FCSTD DOCUMENT  (FreeCAD 0.21R33694 (Git))
Label: asanoha_assembly
License: All rights reserved
LicenseURL: http://en.wikipedia.org/wiki/All_rights_reserved
objects: App::Link×6, App::Part×2
EXTERNAL_REF file=../master_kumiko_box.FCStd obj=Spreadsheet
EXTERNAL_REF file=../parts/kumiko/kumiko_inlay_diagonal.FCStd obj=Body063
EXTERNAL_REF file=../parts/kumiko/kumiko_inlay_hindge.FCStd obj=Body062
EXTERNAL_REF file=../parts/kumiko/kumiko_inlay_short_diagonal.FCStd obj=Body064

FEATURE [App::Link] Link  label="SpreadSheet"
  LinkedObject = -> <external ../master_kumiko_box.FCStd>#Spreadsheet
FEATURE [App::Link] Link001  label="long_diagonal"
  LinkedObject = -> <external ../parts/kumiko/kumiko_inlay_diagonal.FCStd>#Body063
FEATURE [App::Link] Link004  label="hindge_body001"
  LinkPlacement = pos=(2.12132,0,11) rot=(1,1,0;3.14159rad)
  LinkedObject = -> <external ../parts/kumiko/kumiko_inlay_hindge.FCStd>#Body062
  Placement = pos=(2.12132,0,11) rot=(1,1,0;3.14159rad)
  expr: .Placement.Base.x = <<SpreadSheet>>.kumiko_thickness / sqrt(2)
  expr: .Placement.Base.y = 0
  expr: .Placement.Base.z = <<SpreadSheet>>.kumiko_hight
FEATURE [App::Link] Link005  label="short_diagonal001"
  LinkPlacement = pos=(24.5,0,0) rot=(0,0,1;3.14159rad)
  LinkedObject = -> <external ../parts/kumiko/kumiko_inlay_short_diagonal.FCStd>#Body064
  Placement = pos=(24.5,0,0) rot=(0,0,1;3.14159rad)
  expr: .Placement.Base.x = <<SpreadSheet>>.kumiko_grid_size - <<SpreadSheet>>.kumiko_thickness
FEATURE [App::Link] Link006  label="hindge_body002"
  LinkPlacement = pos=(24.5,22.3787,0) rot=(0,0,1;3.14159rad)
  LinkedObject = -> <external ../parts/kumiko/kumiko_inlay_hindge.FCStd>#Body062
  Placement = pos=(24.5,22.3787,0) rot=(0,0,1;3.14159rad)
  expr: .Placement.Base.x = <<SpreadSheet>>.kumiko_grid_size - <<SpreadSheet>>.kumiko_thickness
  expr: .Placement.Base.y = <<SpreadSheet>>.kumiko_grid_size - <<SpreadSheet>>.kumiko_thickness - <<SpreadSheet>>.kumiko_thickness / sqrt(2)
FEATURE [App::Part] Part  label="inlay_top_left"
  Group = -> [Link006,Link005,Link004]
  Origin = -> Origin
  Placement = pos=(0,0,11) rot=(1,1,0;3.14159rad)
  expr: .Placement.Base.z = <<SpreadSheet>>.kumiko_hight
FEATURE [App::Link] Link007  label="inlay_bottom_right"
  LinkedObject = -> Part
FEATURE [App::Part] Part001  label="asanoha"
  Group = -> [Link007,Part,Link001]
  Origin = -> Origin001

RESOLVED EXTERNAL PARTS (link-assembly join: the EXTERNAL_REF files above that resolve inside this repo's crawl, each included once):
---- part ../master_kumiko_box.FCStd = doc fcstd_d57fc246fb5e ----
FCSTD DOCUMENT  (FreeCAD 0.21R33771 (Git))
Label: master_kumiko_box
License: All rights reserved
LicenseURL: https://en.wikipedia.org/wiki/All_rights_reserved
objects: App::Link×3, App::Part×2, Spreadsheet::Sheet×1
EXTERNAL_REF file=assembly/box_assembly.FCStd obj=Part
EXTERNAL_REF file=assembly/lid_assembly.FCStd obj=Part
EXTERNAL_REF file=assembly/kumiko_assembly.FCStd obj=Part001

FEATURE [Spreadsheet::Sheet] Spreadsheet  label="SpreadSheet"
  cells = A1='name; B1='value; C1='calc (y/n); A2='box_length; B2(box_length)=130; C2='n; A3='box_width; B3(box_width)==B2 / 2 + B5 - B13 / 2; C3='n; A4='box_height; B4(box_height)=60; C4='y; A5='box_thickness; B5(box_thickness)=11.5; C5='y; A7='lid_height; B7(lid_height)==B8 * 17 / 8.5; C7='y; A8='lid_frame_width; B8(lid_frame_width)==B5 - B13; C8='y; A9='lid_lip_width; B9(lid_lip_width)==B5 - B8; C9='y; A10='lid_lip_height; B10(lid_lip_hight)=3; C10='y; A12='kumiko_hight; B12(kumiko_hight)==B7 * 11 / 17; C12='y; A13='kumiko_thickness; B13(kumiko_thickness)=3; C13='n; A14='kumiko_grid_size; B14(kumiko_grid_size)==(B2 - 2 * B8 - B13) / 4; C14='y; A16='box_wall_height; B16(box_wall_height)==B4 - B7 - B18; C16='y; A18='floor_edge; B18(floor_edge)=2; C18='n; A20='cnc_spacing; B20(cnc_spacing)=0; C20='y
FEATURE [App::Link] Link  label="box"
  LinkedObject = -> <external assembly/box_assembly.FCStd>#Part
FEATURE [App::Link] Link001  label="lid"
  LinkPlacement = pos=(0,0,43) rot=(0,0,1;0rad)
  LinkedObject = -> <external assembly/lid_assembly.FCStd>#Part
  Placement = pos=(0,0,43) rot=(0,0,1;0rad)
  expr: .Placement.Base.z = <<SpreadSheet>>.box_height - <<SpreadSheet>>.lid_height
FEATURE [App::Link] Link002  label="kumiko_assembly"
  LinkPlacement = pos=(8.5,8.5,49) rot=(0,0,1;0rad)
  LinkedObject = -> <external assembly/kumiko_assembly.FCStd>#Part001
  Placement = pos=(8.5,8.5,49) rot=(0,0,1;0rad)
  expr: .Placement.Base.x = <<SpreadSheet>>.lid_frame_width
  expr: .Placement.Base.y = <<SpreadSheet>>.lid_frame_width
  expr: .Placement.Base.z = <<SpreadSheet>>.box_height - Spreadsheet.kumiko_hight
FEATURE [App::Part] Part  label="lid_complete"
  Group = -> [Link002,Link001]
  Origin = -> Origin
FEATURE [App::Part] Part001  label="kumiko_box_complete"
  Group = -> [Part,Link]
  Origin = -> Origin001
---- part ../parts/kumiko/kumiko_inlay_diagonal.FCStd = doc fcstd_409b1c9e1d78 ----
FCSTD DOCUMENT  (FreeCAD 0.21R33694 (Git))
Label: kumiko_inlay_diagonal
License: All rights reserved
LicenseURL: https://en.wikipedia.org/wiki/All_rights_reserved
objects: Sketcher::SketchObject×1, PartDesign::Pad×1, PartDesign::Body×1, App::Link×1
note: 4 computed .brp shape members not serialized (recipe doc carries the construction recipe); baked Part::Feature solids carry a one-line shape summary decoded from their .brp
EXTERNAL_REF file=../../master_kumiko_box.FCStd obj=Spreadsheet

FEATURE [Sketcher::SketchObject] Sketch098  label="long_diagonal_profile"
  FullyConstrained = true
  MapMode = 5
  Support = -> [XY_Plane084]
  expr: Constraints[10] = <<SpreadSheet>>.kumiko_thickness * sqrt(2) / 2
  expr: Constraints[13] = <<SpreadSheet>>.kumiko_thickness * sqrt(2) / 2
  expr: Constraints[1] = 0
  expr: Constraints[2] = 0
  expr: Constraints[3] = <<SpreadSheet>>.kumiko_thickness * sqrt(2) / 2
  expr: Constraints[6] = <<SpreadSheet>>.kumiko_thickness * sqrt(2) / 2
  expr: Constraints[8] = <<SpreadSheet>>.kumiko_grid_size - <<SpreadSheet>>.kumiko_thickness
  expr: Constraints[9] = <<SpreadSheet>>.kumiko_grid_size - <<SpreadSheet>>.kumiko_thickness
  sketch-geometry (6):
    g0: LineSegment StartX=3.6e-15 StartY=0 StartZ=0 EndX=3.6e-15 EndY=2.12132 EndZ=0
    g1: LineSegment StartX=3.6e-15 StartY=0 StartZ=0 EndX=2.12132 EndY=0 EndZ=0
    g2: LineSegment StartX=24.5 StartY=24.5 StartZ=0 EndX=24.5 EndY=22.3787 EndZ=0
    g3: LineSegment StartX=24.5 StartY=24.5 StartZ=0 EndX=22.3787 EndY=24.5 EndZ=0
    g4: LineSegment StartX=2.12132 StartY=0 StartZ=0 EndX=24.5 EndY=22.3787 EndZ=0
    g5: LineSegment StartX=22.3787 StartY=24.5 StartZ=0 EndX=3.6e-15 EndY=2.12132 EndZ=0
  constraints (18):
    c: Vertical(g0)
    c: DistanceY(g-1,g0) = 0
    c: DistanceX(g-1,g0) = 0
    c: DistanceY(g0,g0) = 2.12132
    c: Coincident(g1,g0)
    c: Horizontal(g1)
    c: DistanceX(g1,g1) = 2.12132
    c: Vertical(g2)
    c: DistanceX(g-1,g2) = 24.5
    c: DistanceY(g-1,g2) = 24.5
    c: DistanceY(g2,g2) = 2.12132
    c: Coincident(g3,g2)
    c: Horizontal(g3)
    c: DistanceX(g3,g3) = 2.12132
    c: Coincident(g4,g1)
    c: Coincident(g4,g2)
    c: Coincident(g5,g3)
    c: Coincident(g5,g0)
FEATURE [PartDesign::Pad] Pad047  label="long_diagonal_extrusion"
  Direction = (0,0,1)
  Length = 11
  Length2 = 10
  Profile = -> Sketch098
  ReferenceAxis = -> Sketch098 [N_Axis]
  Type = 0
  expr: Length = <<SpreadSheet>>.kumiko_hight
FEATURE [PartDesign::Body] Body063  label="long_diagonal_body"
  Group = -> [Sketch098,Pad047]
  Origin = -> Origin084
  Tip = -> Pad047
  expr: .Placement.Base.z = 0
FEATURE [App::Link] Link  label="SpreadSheet"
  LinkedObject = -> <external ../../master_kumiko_box.FCStd>#Spreadsheet
---- part ../parts/kumiko/kumiko_inlay_hindge.FCStd = doc fcstd_16ac07aace51 ----
FCSTD DOCUMENT  (FreeCAD 0.21R33694 (Git))
Label: kumiko_inlay_hindge
License: All rights reserved
LicenseURL: https://en.wikipedia.org/wiki/All_rights_reserved
objects: Sketcher::SketchObject×1, PartDesign::Pad×1, PartDesign::Body×1, App::Link×1
note: 4 computed .brp shape members not serialized (recipe doc carries the construction recipe); baked Part::Feature solids carry a one-line shape summary decoded from their .brp
EXTERNAL_REF file=../../master_kumiko_box.FCStd obj=Spreadsheet

FEATURE [Sketcher::SketchObject] Sketch097  label="hindge_drawing"
  FullyConstrained = true
  MapMode = 5
  Support = -> [XY_Plane083]
  expr: Constraints[0] = 0
  expr: Constraints[11] = <<SpreadSheet>>.kumiko_grid_size * (1 - 1 / sqrt(2)) - 1 / 2 * <<SpreadSheet>>.kumiko_thickness
  expr: Constraints[12] = <<SpreadSheet>>.kumiko_grid_size / sqrt(2) - <<SpreadSheet>>.kumiko_thickness * (1 + 1 / sqrt(2)) * 1 / sqrt(2)
  expr: Constraints[18] = 45
  expr: Constraints[1] = 0
  expr: Constraints[2] = 135 °
  expr: Constraints[4] = 2 * 22.5
  expr: Constraints[6] = <<SpreadSheet>>.kumiko_thickness
  expr: Constraints[7] = (<<SpreadSheet>>.kumiko_grid_size - <<SpreadSheet>>.kumiko_thickness * (1 + sqrt(2) + 1 / sqrt(2 - sqrt(2)))) * 1 / sqrt(2)
  expr: Constraints[8] = (<<SpreadSheet>>.kumiko_grid_size - <<SpreadSheet>>.kumiko_thickness * (1 + sqrt(2) + 1 / sqrt(2 - sqrt(2)))) * (1 - 1 / sqrt(2))
  sketch-geometry (8):
    g0: LineSegment StartX=0 StartY=0 StartZ=0 EndX=2.77164 EndY=2.77164 EndZ=0
    g1: LineSegment StartX=0 StartY=0 StartZ=0 EndX=-2e-16 EndY=3.91969 EndZ=0
    g2: GeomPoint X=4.78519 Y=15.4722 Z=0
    g3: LineSegment StartX=-2e-16 StartY=3.91969 StartZ=0 EndX=4.78519 EndY=15.4722 EndZ=0
    g4: GeomPoint X=6.55456 Y=15.8241 Z=0
    g5: LineSegment StartX=4.78519 StartY=15.4722 StartZ=0 EndX=6.55456 EndY=15.8241 EndZ=0
    g6: LineSegment StartX=2.77164 StartY=2.77164 StartZ=0 EndX=7.70261 EndY=14.6761 EndZ=0
    g7: LineSegment StartX=6.55456 StartY=15.8241 StartZ=0 EndX=7.70261 EndY=14.6761 EndZ=0
  constraints (20):
    c: DistanceX(g-1,g0) = 0
    c: DistanceY(g-1,g0) = 0
    c: Angle(g0,g-1) = 2.35619
    c: Coincident(g1,g0)
    c: Angle(g0,g1) = 0.785398
    c: Equal(g1,g0)
    c: Distance(g0,g1) = 3
    c: DistanceY(g1,g2) = 11.5525
    c: DistanceX(g1,g2) = 4.78519
    c: Coincident(g3,g1)
    c: Coincident(g3,g2)
    c: DistanceX(g0,g4) = 6.55456
    c: DistanceY(g0,g4) = 15.8241
    c: Coincident(g5,g3)
    c: Coincident(g5,g4)
    c: Coincident(g6,g0)
    c: Parallel(g3,g6)
    c: Coincident(g7,g5)
    c: Angle(g7,g-1) = 0.785398
    c: Coincident(g7,g6)
FEATURE [PartDesign::Pad] Pad049  label="hindge_extrude"
  Direction = (0,0,1)
  Length = 11
  Length2 = 10
  Profile = -> Sketch097
  ReferenceAxis = -> Sketch097 [N_Axis]
  Type = 0
  expr: Length = <<SpreadSheet>>.kumiko_hight
FEATURE [PartDesign::Body] Body062  label="hindge_body"
  Group = -> [Sketch097,Pad049]
  Origin = -> Origin083
  Tip = -> Pad049
  expr: .Placement.Base.z = 0
FEATURE [App::Link] Link  label="SpreadSheet"
  LinkedObject = -> <external ../../master_kumiko_box.FCStd>#Spreadsheet
---- part ../parts/kumiko/kumiko_inlay_short_diagonal.FCStd = doc fcstd_d7b73f897647 ----
FCSTD DOCUMENT  (FreeCAD 0.21R33694 (Git))
Label: kumiko_inlay_short_diagonal
License: All rights reserved
LicenseURL: https://en.wikipedia.org/wiki/All_rights_reserved
objects: Sketcher::SketchObject×1, PartDesign::Pad×1, PartDesign::Body×1, App::Link×1
note: 4 computed .brp shape members not serialized (recipe doc carries the construction recipe); baked Part::Feature solids carry a one-line shape summary decoded from their .brp
EXTERNAL_REF file=../../master_kumiko_box.FCStd obj=Spreadsheet

FEATURE [Sketcher::SketchObject] Sketch099  label="short_diagonal_drawing"
  FullyConstrained = true
  MapMode = 5
  Support = -> [XY_Plane085]
  expr: Constraints[0] = 0
  expr: Constraints[10] = <<SpreadSheet>>.kumiko_thickness / sqrt(2)
  expr: Constraints[11] = (<<SpreadSheet>>.kumiko_grid_size - <<SpreadSheet>>.kumiko_thickness * (1 + sqrt(2) + 1 / sqrt(2 - sqrt(2)))) * (1 - 1 / sqrt(2))
  expr: Constraints[12] = (<<SpreadSheet>>.kumiko_grid_size - <<SpreadSheet>>.kumiko_thickness * (1 + sqrt(2) + 1 / sqrt(2 - sqrt(2)))) * (1 - 1 / sqrt(2))
  expr: Constraints[21] = 0 mm
  expr: Constraints[3] = <<SpreadSheet>>.kumiko_thickness * sqrt(2) / 2
  expr: Constraints[4] = <<SpreadSheet>>.kumiko_grid_size * (1 - 1 / sqrt(2)) - 1 / 2 * <<SpreadSheet>>.kumiko_thickness
  expr: Constraints[5] = <<SpreadSheet>>.kumiko_grid_size * (1 - 1 / sqrt(2)) - 1 / 2 * <<SpreadSheet>>.kumiko_thickness
  expr: Constraints[6] = (<<SpreadSheet>>.kumiko_grid_size - <<SpreadSheet>>.kumiko_thickness * (1 + sqrt(2) + 1 / sqrt(2 - sqrt(2)))) * (1 - 1 / sqrt(2))
  expr: Constraints[7] = (<<SpreadSheet>>.kumiko_grid_size - <<SpreadSheet>>.kumiko_thickness * (1 + sqrt(2) + 1 / sqrt(2 - sqrt(2)))) * (1 - 1 / sqrt(2))
  sketch-geometry (10):
    g0: GeomPoint X=0 Y=0 Z=0
    g1: LineSegment StartX=0 StartY=0 StartZ=0 EndX=0 EndY=-2.12132 EndZ=0
    g2: GeomPoint X=6.55456 Y=-6.55456 Z=0
    g3: GeomPoint X=4.78519 Y=-6.90651 Z=0
    g4: LineSegment StartX=0 StartY=0 StartZ=0 EndX=2.12132 EndY=0 EndZ=0
    g5: GeomPoint X=6.90651 Y=-4.78519 Z=0
    g6: LineSegment StartX=6.90651 StartY=-4.78519 StartZ=0 EndX=2.12132 EndY=0 EndZ=0
    g7: LineSegment StartX=6.90651 StartY=-4.78519 StartZ=0 EndX=6.55456 EndY=-6.55456 EndZ=0
    g8: LineSegment StartX=6.55456 StartY=-6.55456 StartZ=0 EndX=4.78519 EndY=-6.90651 EndZ=0
    g9: LineSegment StartX=4.78519 StartY=-6.90651 StartZ=0 EndX=0 EndY=-2.12132 EndZ=0
  constraints (22):
    c: DistanceX(g-1,g0) = 0
    c: Coincident(g1,g0)
    c: Vertical(g1)
    c: DistanceY(g1,g1) = 2.12132
    c: DistanceX(g1,g2) = 6.55456
    c: DistanceY(g2,g1) = 6.55456
    c: DistanceY(g3,g1) = 4.78519
    c: DistanceX(g1,g3) = 4.78519
    c: Coincident(g4,g1)
    c: Horizontal(g4)
    c: DistanceX(g4,g4) = 2.12132
    c: DistanceX(g4,g5) = 4.78519
    c: DistanceY(g5,g4) = 4.78519
    c: Coincident(g6,g5)
    c: Coincident(g6,g4)
    c: Coincident(g7,g6)
    c: Coincident(g7,g2)
    c: Coincident(g8,g7)
    c: Coincident(g8,g3)
    c: Coincident(g9,g8)
    c: Coincident(g9,g1)
    c: DistanceY(g-1,g1) = 0
FEATURE [PartDesign::Pad] Pad048  label="short_diagnoal_extrude"
  Direction = (0,0,1)
  Length = 11
  Length2 = 10
  Profile = -> Sketch099
  ReferenceAxis = -> Sketch099 [N_Axis]
  Type = 0
  expr: Length = <<SpreadSheet>>.kumiko_hight
FEATURE [PartDesign::Body] Body064  label="short_diagonal"
  Group = -> [Sketch099,Pad048]
  Origin = -> Origin085
  Tip = -> Pad048
  expr: .Placement.Base.z = 0
FEATURE [App::Link] Link  label="SpreadSheet"
  LinkedObject = -> <external ../../master_kumiko_box.FCStd>#Spreadsheet
